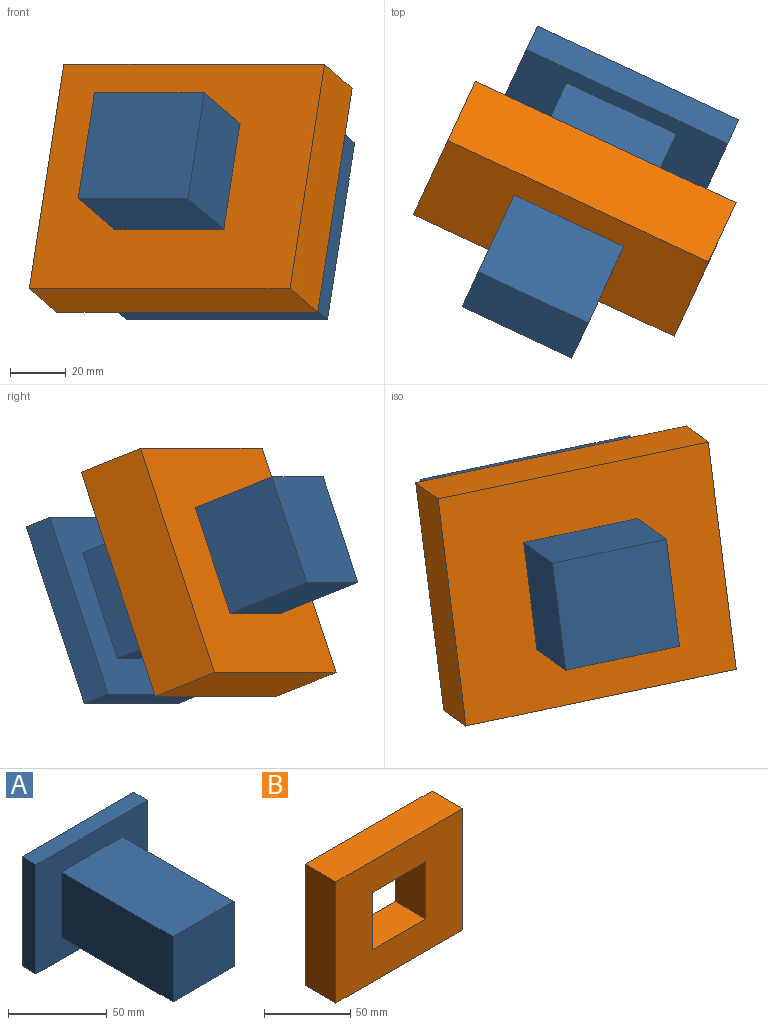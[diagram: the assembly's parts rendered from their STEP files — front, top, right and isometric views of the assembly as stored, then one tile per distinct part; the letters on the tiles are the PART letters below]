
ASSEMBLY  parts=2 mates=1
PART A: 11 faces, bbox 80x90x67.7 mm
  f0: plane 80x43.62mm, normal (0,0,-1), area 3489.2mm2, adj f1,f3,f4,f10
  f1: plane 80x40.44mm, normal (1,0,0), area 3234.8mm2, adj f0,f2,f4,f10
  f2: plane 80x43.62mm, normal (0,0,1), area 3489.2mm2, adj f1,f3,f4,f10
  f3: plane 80x40.44mm, normal (-1,0,0), area 3234.8mm2, adj f0,f2,f4,f10
  f4: plane 43.62x40.44mm, normal (0,-1,0), area 1763.6mm2, adj f0,f1,f2,f3
  f5: plane 79.96x10mm, normal (0,0,-1), area 799.6mm2, adj f6,f8,f9,f10
  f6: plane 67.69x10mm, normal (1,0,0), area 676.9mm2, adj f5,f7,f9,f10
  f7: plane 79.96x10mm, normal (0,0,1), area 799.6mm2, adj f6,f8,f9,f10
  f8: plane 67.69x10mm, normal (-1,0,0), area 676.9mm2, adj f5,f7,f9,f10
  f9: plane 79.96x67.69mm, normal (0,1,0), area 5413mm2, adj f5,f6,f7,f8
  f10: plane 79.96x67.69mm, normal (0,-1,0), area 3649.4mm2, adj f0,f1,f2,f3,f5,f6,f7,f8
PART B: 10 faces, bbox 103.6x25x85.9 mm
  f0: plane 40.44x25mm, normal (-1,0,0), area 1010.9mm2, adj f1,f7,f8,f9
  f1: plane 43.62x25mm, normal (0,0,1), area 1090.4mm2, adj f0,f2,f8,f9
  f2: plane 40.44x25mm, normal (1,0,0), area 1010.9mm2, adj f1,f7,f8,f9
  f3: plane 103.59x25mm, normal (0,0,-1), area 2589.7mm2, adj f4,f6,f8,f9
  f4: plane 85.87x25mm, normal (1,0,0), area 2146.7mm2, adj f3,f5,f8,f9
  f5: plane 103.59x25mm, normal (0,0,1), area 2589.7mm2, adj f4,f6,f8,f9
  f6: plane 85.87x25mm, normal (-1,0,0), area 2146.7mm2, adj f3,f5,f8,f9
  f7: plane 43.62x25mm, normal (0,0,-1), area 1090.4mm2, adj f0,f2,f8,f9
  f8: plane 103.59x85.87mm, normal (0,-1,0), area 7131.2mm2, adj f0,f1,f2,f3,f4,f5,f6,f7
  f9: plane 103.59x85.87mm, normal (0,1,0), area 7131.2mm2, adj f0,f1,f2,f3,f4,f5,f6,f7
PLACE A rot(axis=(-0.62,0.14,-0.78),31.9deg) t=(36.54,-1.9,-38.31)mm
PLACE B rot(axis=(0.98,-0.22,-0.04),160.5deg) t=(17.64,-42.42,-22.04)mm
MATE slider B.f8 <-> A.f4  axis (0.4,0.85,-0.34) through (27.57,-21.13,-30.59)mm
